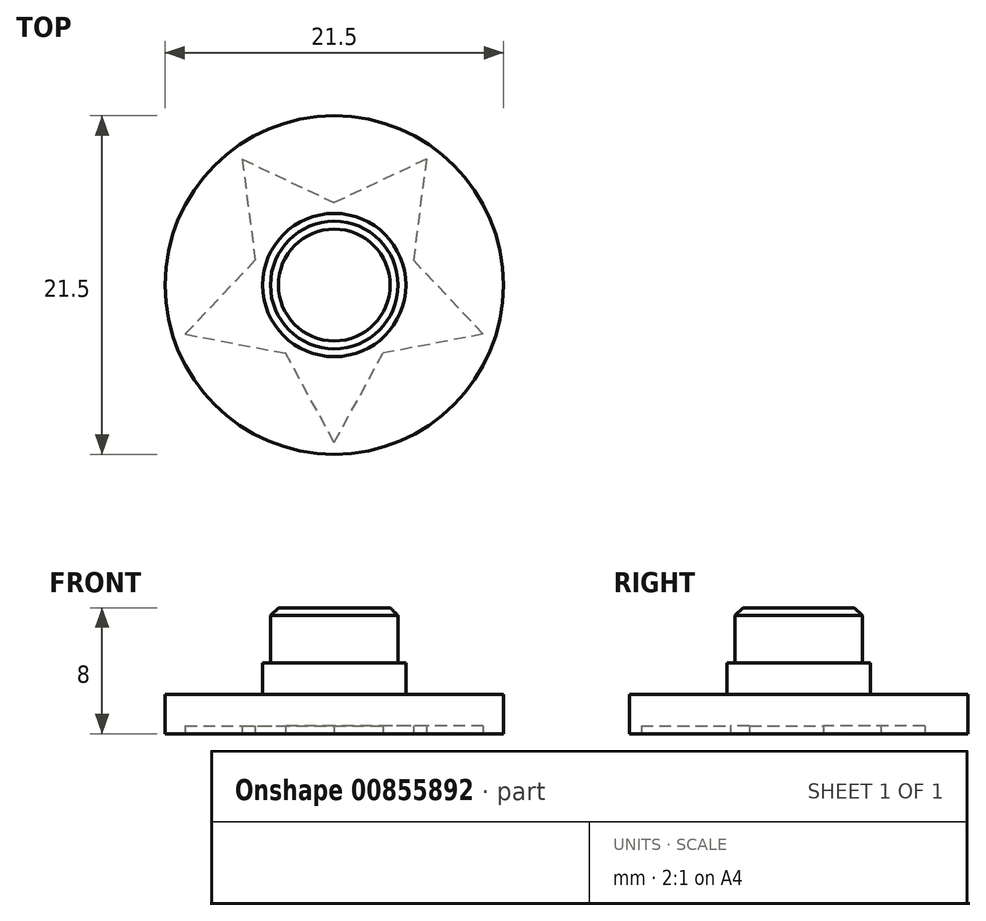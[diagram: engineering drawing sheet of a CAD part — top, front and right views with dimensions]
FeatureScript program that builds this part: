
annotation { "Feature Type Name" : "Feature", "Feature Type Description" : "" }
export const myFeature = defineFeature(function(context is Context, id is Id, definition is map)
    precondition{}
    {
        {
            var Q0;
            Q0=qCreatedBy(makeId("Top.planeOp"),FACE);
            var sketch = newSketch(context, id + "F0", { "sketchPlane" : qUnion([Q0])});
            skCircle(sketch, "E0", {"center": v(0, 0) * mm, "radius": 10 * mm});
            skLineSegment(sketch, "E1", {"start": v(0, 25) * mm, "end": v(0, -25) * mm, "construction": true});
            skLineSegment(sketch, "E2", {"start": v(-25, 0) * mm, "end": v(25, 0) * mm, "construction": true});
            skLineSegment(sketch, "E3", {"start": v(-17.68, 17.68) * mm, "end": v(0, 0) * mm, "construction": true});
            skLineSegment(sketch, "E4", {"start": v(0, 0) * mm, "end": v(17.68, -17.68) * mm, "construction": true});
            skLineSegment(sketch, "E5", {"start": v(0, 0) * mm, "end": v(17.68, 17.68) * mm, "construction": true});
            skLineSegment(sketch, "E6", {"start": v(0, 0) * mm, "end": v(-17.68, -17.68) * mm, "construction": true});
            skLineSegment(sketch, "E7", {"start": v(0, 0) * mm, "end": v(-7.65, 18.48) * mm, "construction": true});
            skLineSegment(sketch, "E8", {"start": v(0, 0) * mm, "end": v(-18.48, -7.65) * mm, "construction": true});
            skLineSegment(sketch, "E9", {"start": v(0, 0) * mm, "end": v(-7.65, -18.48) * mm, "construction": true});
            skLineSegment(sketch, "E10", {"start": v(0, 0) * mm, "end": v(7.65, -18.48) * mm, "construction": true});
            skLineSegment(sketch, "E11", {"start": v(0, 0) * mm, "end": v(18.48, -7.65) * mm, "construction": true});
            skLineSegment(sketch, "E12", {"start": v(0, 0) * mm, "end": v(18.48, 7.65) * mm, "construction": true});
            skLineSegment(sketch, "E13", {"start": v(0, 0) * mm, "end": v(7.65, 18.48) * mm, "construction": true});
            skLineSegment(sketch, "E14", {"start": v(0, 0) * mm, "end": v(-18.48, 7.65) * mm, "construction": true});
            skCircle(sketch, "E15", {"center": v(0, 0) * mm, "radius": 5 * mm, "construction": true});
            skLineSegment(sketch, "E16", {"start": v(0, -10) * mm, "end": v(-3.1, -4.32) * mm});
            skLineSegment(sketch, "E17", {"start": v(0, -10) * mm, "end": v(3.1, -4.32) * mm});
            skLineSegment(sketch, "E18.1.0", {"start": v(9.46, -3.13) * mm, "end": v(3.1, -4.32) * mm});
            skLineSegment(sketch, "E18.1.1", {"start": v(9.46, -3.13) * mm, "end": v(5.02, 1.58) * mm});
            skLineSegment(sketch, "E18.2.0", {"start": v(5.85, 8) * mm, "end": v(5.02, 1.58) * mm});
            skLineSegment(sketch, "E18.2.1", {"start": v(5.85, 8) * mm, "end": v(0, 5.23) * mm});
            skLineSegment(sketch, "E18.3.0", {"start": v(-5.85, 8) * mm, "end": v(0, 5.23) * mm});
            skLineSegment(sketch, "E18.3.1", {"start": v(-5.85, 8) * mm, "end": v(-5.02, 1.58) * mm});
            skLineSegment(sketch, "E18.4.0", {"start": v(-9.46, -3.13) * mm, "end": v(-5.02, 1.58) * mm});
            skLineSegment(sketch, "E18.4.1", {"start": v(-9.46, -3.13) * mm, "end": v(-3.1, -4.32) * mm});
            skPoint(sketch, "E18.center", {"position": v(0, -0.05) * mm});
            skPoint(sketch, "E19.orphan", {"position": v(-3.54, -3.54) * mm});
            skPoint(sketch, "E20.orphan", {"position": v(-2.22, -4.5) * mm});
            skPoint(sketch, "E21.orphan", {"position": v(2.22, -4.5) * mm});
            skPoint(sketch, "E22.orphan", {"position": v(3.54, -3.54) * mm});
            skPoint(sketch, "E23.orphan", {"position": v(4.9, 0.7) * mm});
            skPoint(sketch, "E24.orphan", {"position": v(0.81, 4.85) * mm});
            skPoint(sketch, "E25.orphan", {"position": v(-0.81, 4.85) * mm});
            skPoint(sketch, "E26.orphan", {"position": v(-4.9, 0.7) * mm});
            skCircle(sketch, "E27", {"center": v(0, 0) * mm, "radius": 10.75 * mm});
            skSolve(sketch);
        }
        {
            var Q0;
            Q0=qSketchRegion(id+"F0",true);
            var Q1;
            Q1=makeQuery(id+"F0.imprint","IMPRINT",FACE,{"disambiguationData":[TD([[makeQuery(id+"F0.imprint","IMPRINT",EDGE,{"derivedFrom":sQuery(id+"F0.wireOp",EDGE,"E0")}),1.0]])]});
            var Q2;
            Q2=makeQuery(id+"F0.imprint","IMPRINT",FACE,{"disambiguationData":[TD([[makeQuery(id+"F0.imprint","IMPRINT",EDGE,{"derivedFrom":sQuery(id+"F0.wireOp",EDGE,"E16")}),-1.0]])]});
            extrude(context, id + "F1", {"entities" : qUnion([Q0, Q1, Q2]), "depth" : 2.5 * mm, "offsetDistance" : 25 * mm});
        }
        {
            var Q0;
            Q0=makeQuery(id+"F1.opExtrude","CAP_FACE",FACE,{"disambiguationData":[OSD([sQuery(id+"F0.wireOp",EDGE,"E27")])],"isStart":false});
            var sketch = newSketch(context, id + "F2", { "sketchPlane" : qUnion([Q0])});
            skCircle(sketch, "E28", {"center": v(0, 0) * mm, "radius": 4.05 * mm});
            skSolve(sketch);
        }
        {
            var Q0;
            Q0=qSketchRegion(id+"F2",true);
            extrude(context, id + "F3", {"entities" : qUnion([Q0]), "operationType" : NewBodyOperationType.ADD, "depth" : 5.5 * mm, "offsetDistance" : 25 * mm});
        }
        {
            var Q0;
            Q0=makeQuery(id+"F3.opExtrude","CAP_EDGE",EDGE,{"disambiguationData":[OSD([sQuery(id+"F2.wireOp",EDGE,"E28")])],"isStart":false});
            var Q1;
            Q1=makeQuery(id+"F1.opExtrude","CAP_EDGE",EDGE,{"disambiguationData":[OSD([sQuery(id+"F0.wireOp",EDGE,"281bee0e-2aea-47b7-b4e1-999b86a55542.4.0")])],"isStart":true});
            var Q2;
            Q2=makeQuery(id+"F1.opExtrude","CAP_EDGE",EDGE,{"disambiguationData":[OSD([sQuery(id+"F0.wireOp",EDGE,"281bee0e-2aea-47b7-b4e1-999b86a55542.3.1")])],"isStart":true});
            var Q3;
            Q3=makeQuery(id+"F1.opExtrude","CAP_EDGE",EDGE,{"disambiguationData":[OSD([sQuery(id+"F0.wireOp",EDGE,"281bee0e-2aea-47b7-b4e1-999b86a55542.3.0")])],"isStart":true});
            var Q4;
            Q4=makeQuery(id+"F1.opExtrude","CAP_EDGE",EDGE,{"disambiguationData":[OSD([sQuery(id+"F0.wireOp",EDGE,"281bee0e-2aea-47b7-b4e1-999b86a55542.2.1")])],"isStart":true});
            var Q5;
            Q5=makeQuery(id+"F1.opExtrude","CAP_EDGE",EDGE,{"disambiguationData":[OSD([sQuery(id+"F0.wireOp",EDGE,"281bee0e-2aea-47b7-b4e1-999b86a55542.2.0")])],"isStart":true});
            var Q6;
            Q6=makeQuery(id+"F1.opExtrude","CAP_EDGE",EDGE,{"disambiguationData":[OSD([sQuery(id+"F0.wireOp",EDGE,"281bee0e-2aea-47b7-b4e1-999b86a55542.1.1")])],"isStart":true});
            var Q7;
            Q7=makeQuery(id+"F1.opExtrude","CAP_EDGE",EDGE,{"disambiguationData":[OSD([sQuery(id+"F0.wireOp",EDGE,"281bee0e-2aea-47b7-b4e1-999b86a55542.1.0")])],"isStart":true});
            var Q8;
            Q8=makeQuery(id+"F1.opExtrude","CAP_EDGE",EDGE,{"disambiguationData":[OSD([sQuery(id+"F0.wireOp",EDGE,"VJwDG1Qv-JdYY-zPm5-o4WR-dzW4zfFZ494p")])],"isStart":true});
            var Q9;
            Q9=makeQuery(id+"F1.opExtrude","CAP_EDGE",EDGE,{"disambiguationData":[OSD([sQuery(id+"F0.wireOp",EDGE,"Lo3pglTx-e1UP-W00b-ypUq-am2WEzU7Gj5O")])],"isStart":true});
            var Q10;
            Q10=makeQuery(id+"F1.opExtrude","CAP_EDGE",EDGE,{"disambiguationData":[OSD([sQuery(id+"F0.wireOp",EDGE,"281bee0e-2aea-47b7-b4e1-999b86a55542.5.1")])],"isStart":true});
            var Q11;
            Q11=makeQuery(id+"F1.opExtrude","CAP_EDGE",EDGE,{"disambiguationData":[OSD([sQuery(id+"F0.wireOp",EDGE,"281bee0e-2aea-47b7-b4e1-999b86a55542.5.0")])],"isStart":true});
            var Q12;
            Q12=makeQuery(id+"F1.opExtrude","CAP_EDGE",EDGE,{"disambiguationData":[OSD([sQuery(id+"F0.wireOp",EDGE,"281bee0e-2aea-47b7-b4e1-999b86a55542.4.1")])],"isStart":true});
            chamfer(context, id + "F4", {"entities" : qUnion([Q0, Q1, Q2, Q3, Q4, Q5, Q6, Q7, Q8, Q9, Q10, Q11, Q12]), "width" : 0.5 * mm, "tangentPropagation" : true});
        }
        {
            var Q0;
            Q0=makeQuery(id+"F1.opExtrude","CAP_FACE",FACE,{"disambiguationData":[OSD([sQuery(id+"F0.wireOp",EDGE,"E27")])],"isStart":false});
            var sketch = newSketch(context, id + "F5", { "sketchPlane" : qUnion([Q0])});
            skCircle(sketch, "E29", {"center": v(0, 0) * mm, "radius": 4.55 * mm});
            skSolve(sketch);
        }
        {
            var Q0;
            Q0=qSketchRegion(id+"F5",true);
            extrude(context, id + "F6", {"entities" : qUnion([Q0]), "operationType" : NewBodyOperationType.ADD, "depth" : 2 * mm, "offsetDistance" : 25 * mm});
        }
        {
            var Q0;
            Q0=makeQuery(id+"F0.imprint","IMPRINT",FACE,{"disambiguationData":[TD([[makeQuery(id+"F0.imprint","IMPRINT",EDGE,{"derivedFrom":sQuery(id+"F0.wireOp",EDGE,"E16")}),-1.0]])]});
            extrude(context, id + "F7", {"entities" : qUnion([Q0]), "operationType" : NewBodyOperationType.REMOVE, "depth" : 0.5 * mm, "offsetDistance" : 25 * mm});
        }
    });
